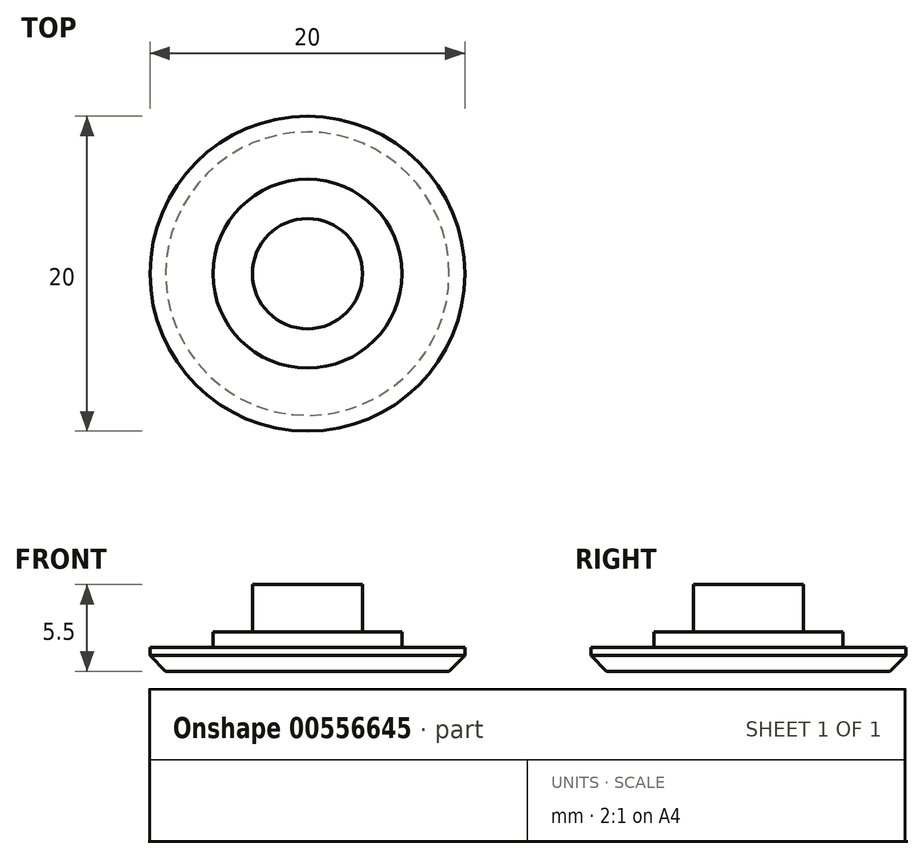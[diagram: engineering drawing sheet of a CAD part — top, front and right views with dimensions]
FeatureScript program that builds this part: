
annotation { "Feature Type Name" : "Feature", "Feature Type Description" : "" }
export const myFeature = defineFeature(function(context is Context, id is Id, definition is map)
    precondition{}
    {
        {
            var Q0;
            Q0=qCreatedBy(makeId("Top.planeOp"),FACE);
            var sketch = newSketch(context, id + "F0", { "sketchPlane" : qUnion([Q0])});
            skCircle(sketch, "E0", {"center": v(0, 0) * mm, "radius": 3.5 * mm});
            skCircle(sketch, "E1", {"center": v(0, 0) * mm, "radius": 6 * mm});
            skCircle(sketch, "E2", {"center": v(0, 0) * mm, "radius": 10 * mm});
            skSolve(sketch);
        }
        {
            var Q0;
            Q0 = qSketchRegion(id + "F0", true);
            extrude(context, id + "F1", {"entities" : qUnion([Q0]), "depth" : 1.5 * mm, "offsetDistance" : 25 * mm});
        }
        {
            var Q0;
            Q0=makeQuery(id+"F0.imprint","IMPRINT",FACE,{"disambiguationData":[TD([[makeQuery(id+"F0.imprint","IMPRINT",EDGE,{"derivedFrom":sQuery(id+"F0.wireOp",EDGE,"E0")}),-1.0]])]});
            extrude(context, id + "F2", {"entities" : qUnion([Q0]), "operationType" : NewBodyOperationType.ADD, "depth" : 2.5 * mm, "offsetDistance" : 25 * mm});
        }
        {
            var Q0;
            Q0=makeQuery(id+"F0.imprint","IMPRINT",FACE,{"disambiguationData":[TD([[makeQuery(id+"F0.imprint","IMPRINT",EDGE,{"derivedFrom":sQuery(id+"F0.wireOp",EDGE,"E0")}),1.0]])]});
            extrude(context, id + "F3", {"entities" : qUnion([Q0]), "operationType" : NewBodyOperationType.ADD, "depth" : 5.5 * mm, "offsetDistance" : 25 * mm});
        }
        {
            var Q0;
            Q0=makeQuery(id+"F1.opExtrude","CAP_EDGE",EDGE,{"disambiguationData":[OSD([sQuery(id+"F0.wireOp",EDGE,"E2")])],"isStart":true});
            chamfer(context, id + "F4", {"entities" : qUnion([Q0]), "width" : 1 * mm, "tangentPropagation" : true});
        }
    });
